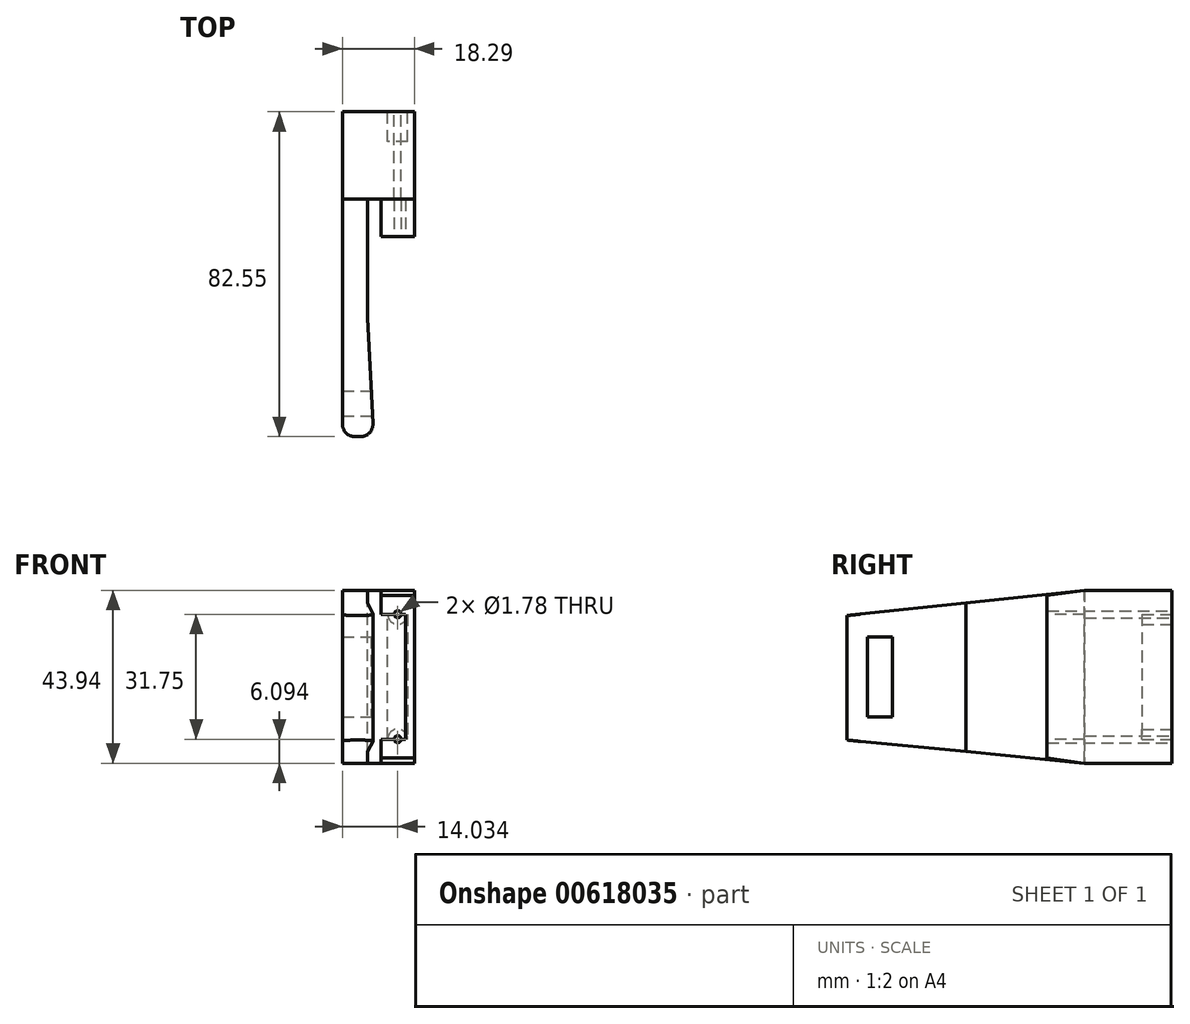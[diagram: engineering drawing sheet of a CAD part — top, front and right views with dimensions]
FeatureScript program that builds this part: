
annotation { "Feature Type Name" : "Feature", "Feature Type Description" : "" }
export const myFeature = defineFeature(function(context is Context, id is Id, definition is map)
    precondition{}
    {
        {
            var Q0;
            Q0=qCreatedBy(makeId("Right.planeOp"),FACE);
            var sketch = newSketch(context, id + "F0", { "sketchPlane" : qUnion([Q0])});
            skLineSegment(sketch, "E0", {"start": v(0, 0) * mm, "end": v(0, -43.94) * mm});
            skLineSegment(sketch, "E1", {"start": v(0, -43.94) * mm, "end": v(31.75, -43.94) * mm});
            skLineSegment(sketch, "E2", {"start": v(31.75, -43.94) * mm, "end": v(31.75, 0) * mm});
            skLineSegment(sketch, "E3", {"start": v(31.75, 0) * mm, "end": v(0, 0) * mm});
            skSolve(sketch);
        }
        {
            var Q0;
            Q0=qSketchRegion(id+"F0",true);
            extrude(context, id + "F1", {"entities" : qUnion([Q0]), "depth" : 8.5 * mm});
        }
        {
            var Q0;
            Q0=makeQuery(id+"F1.opExtrude","CAP_FACE",FACE,{"disambiguationData":[OSD([sQuery(id+"F0.wireOp",EDGE,"E0"),sQuery(id+"F0.wireOp",EDGE,"E1"),sQuery(id+"F0.wireOp",EDGE,"E2"),sQuery(id+"F0.wireOp",EDGE,"E3")])],"isStart":true});
            var sketch = newSketch(context, id + "F2", { "sketchPlane" : qUnion([Q0])});
            skLineSegment(sketch, "E4", {"start": v(-31.75, 0) * mm, "end": v(-9.53, 0) * mm});
            skLineSegment(sketch, "E5", {"start": v(-31.75, -21.97) * mm, "end": v(-9.53, -21.97) * mm});
            skLineSegment(sketch, "E6", {"start": v(0, -1.33) * mm, "end": v(0, -42.6) * mm});
            skLineSegment(sketch, "E7", {"start": v(0, -1.33) * mm, "end": v(-9.53, 0) * mm});
            skLineSegment(sketch, "E8", {"start": v(-31.75, -43.94) * mm, "end": v(-9.53, -43.94) * mm});
            skLineSegment(sketch, "E9", {"start": v(-9.53, -43.94) * mm, "end": v(0, -42.6) * mm});
            skSolve(sketch);
        }
        {
            var Q0;
            {var subQ0=sQuery(id+"F2.wireOp",EDGE,"E7");Q0=makeQuery(id+"F2.imprint","IMPRINT",FACE,{"disambiguationData":[TD([[makeQuery(id+"F2.imprint","IMPRINT",EDGE,{"derivedFrom":subQ0}),-1.0]])]});}
            var Q1;
            {var subQ0=sQuery(id+"F2.wireOp",EDGE,"E9");Q1=makeQuery(id+"F2.imprint","IMPRINT",FACE,{"disambiguationData":[TD([[makeQuery(id+"F2.imprint","IMPRINT",EDGE,{"derivedFrom":subQ0}),-1.0]])]});}
            extrude(context, id + "F3", {"entities" : qUnion([Q0, Q1]), "operationType" : NewBodyOperationType.REMOVE, "oppositeDirection" : true, "depth" : 25.4 * mm});
        }
        {
            var Q0;
            Q0=makeQuery(id+"F1.opExtrude","SWEPT_FACE",FACE,{"disambiguationData":[OSD([sQuery(id+"F0.wireOp",EDGE,"E2")])]});
            var sketch = newSketch(context, id + "F4", { "sketchPlane" : qUnion([Q0])});
            skCircle(sketch, "E10", {"center": v(-4.25, -37.85) * mm, "radius": 0.89 * mm});
            skCircle(sketch, "E11", {"center": v(-4.25, -6.1) * mm, "radius": 0.89 * mm});
            skSolve(sketch);
        }
        {
            var Q0;
            Q0=makeQuery(id+"F4.imprint","IMPRINT",FACE,{"disambiguationData":[TD([[makeQuery(id+"F4.imprint","IMPRINT",EDGE,{"derivedFrom":sQuery(id+"F4.wireOp",EDGE,"E10")}),1.0]])]});
            var Q1;
            Q1=makeQuery(id+"F4.imprint","IMPRINT",FACE,{"disambiguationData":[TD([[makeQuery(id+"F4.imprint","IMPRINT",EDGE,{"derivedFrom":sQuery(id+"F4.wireOp",EDGE,"E11")}),1.0]])]});
            extrude(context, id + "F5", {"entities" : qUnion([Q0, Q1]), "operationType" : NewBodyOperationType.REMOVE, "oppositeDirection" : true, "depth" : 31.75 * mm});
        }
        {
            var Q0;
            Q0=makeQuery(id+"F1.opExtrude","SWEPT_FACE",FACE,{"disambiguationData":[OSD([sQuery(id+"F0.wireOp",EDGE,"E0")])]});
            var sketch = newSketch(context, id + "F6", { "sketchPlane" : qUnion([Q0])});
            skLineSegment(sketch, "E12", {"start": v(4.25, -37.85) * mm, "end": v(0, -37.85) * mm});
            skLineSegment(sketch, "E13", {"start": v(4.25, -37.85) * mm, "end": v(8.5, -37.85) * mm});
            skLineSegment(sketch, "E14", {"start": v(4.25, -6.1) * mm, "end": v(0, -6.1) * mm});
            skLineSegment(sketch, "E15", {"start": v(4.25, -6.1) * mm, "end": v(8.5, -6.1) * mm});
            skPoint(sketch, "E16.endSnap0", {"position": v(8.5, -21.97) * mm});
            skLineSegment(sketch, "E17", {"start": v(6.29, -21.97) * mm, "end": v(6.29, -37.85) * mm});
            skLineSegment(sketch, "E18", {"start": v(6.29, -21.97) * mm, "end": v(6.29, -6.1) * mm});
            skSolve(sketch);
        }
        {
            var Q0;
            Q0=qSketchRegion(id+"F6",true);
            var Q1;
            {var subQ4=sQuery(id+"F6.wireOp",EDGE,"E17");Q1=makeQuery(id+"F6.imprint","IMPRINT",FACE,{"disambiguationData":[TD([[makeQuery(id+"F6.imprint","IMPRINT",EDGE,{"derivedFrom":subQ4}),-1.0]])]});}
            extrude(context, id + "F7", {"entities" : qUnion([Q0, Q1]), "operationType" : NewBodyOperationType.REMOVE, "oppositeDirection" : true, "depth" : 9.52 * mm});
        }
        {
            var Q0;
            Q0=makeQuery(id+"F1.opExtrude","CAP_FACE",FACE,{"disambiguationData":[OSD([sQuery(id+"F0.wireOp",EDGE,"E0"),sQuery(id+"F0.wireOp",EDGE,"E1"),sQuery(id+"F0.wireOp",EDGE,"E2"),sQuery(id+"F0.wireOp",EDGE,"E3")])],"isStart":true});
            var sketch = newSketch(context, id + "F8", { "sketchPlane" : qUnion([Q0])});
            skLineSegment(sketch, "E19", {"start": v(-9.52, -6.1) * mm, "end": v(-9.53, 0) * mm});
            skLineSegment(sketch, "E20", {"start": v(-9.53, -37.85) * mm, "end": v(-9.53, -43.94) * mm});
            skSolve(sketch);
        }
        {
            var Q0;
            Q0=makeQuery(id+"F8.imprint","IMPRINT",FACE,{"disambiguationData":[TD([[makeQuery(id+"F8.imprint","IMPRINT",EDGE,{"derivedFrom":sQuery(id+"F8.wireOp",EDGE,"E19")}),1.0]])]});
            extrude(context, id + "F9", {"entities" : qUnion([Q0]), "operationType" : NewBodyOperationType.ADD, "depth" : 3.43 * mm});
        }
        {
            var Q0;
            Q0=makeQuery(id+"F9.opExtrude","CAP_FACE",FACE,{"disambiguationData":[OSD([sQuery(id+"F0.wireOp",EDGE,"E0"),sQuery(id+"F0.wireOp",EDGE,"E1"),sQuery(id+"F0.wireOp",EDGE,"E2"),sQuery(id+"F0.wireOp",EDGE,"E3"),sQuery(id+"F8.wireOp",EDGE,"E19"),sQuery(id+"F8.wireOp",EDGE,"E20")])],"isStart":false});
            extrude(context, id + "F10", {"entities" : qUnion([Q0]), "operationType" : NewBodyOperationType.ADD, "depth" : 6.35 * mm, "offsetDistance" : 25.4 * mm});
        }
        {
            var Q0;
            {var subQ0=sQuery(id+"F8.wireOp",EDGE,"E20");var subQ1=sQuery(id+"F8.wireOp",EDGE,"E19");var subQ2=sQuery(id+"F0.wireOp",EDGE,"E0");Q0=makeQuery(id+"F10.boolean.opBoolean","MERGE",FACE,{"derivedFrom":[makeQuery(id+"F9.boolean.opBoolean","MERGE",FACE,{"derivedFrom":[makeQuery(id+"F7.boolean.opBoolean","COPY",FACE,{"derivedFrom":makeQuery(id+"F7.opExtrude","CAP_FACE",FACE,{"disambiguationData":[OSD([subQ2,sQuery(id+"F4.wireOp",EDGE,"E10"),sQuery(id+"F4.wireOp",EDGE,"E11"),sQuery(id+"F6.wireOp",EDGE,"E12"),sQuery(id+"F6.wireOp",EDGE,"E13"),sQuery(id+"F6.wireOp",EDGE,"E14"),sQuery(id+"F6.wireOp",EDGE,"E15"),sQuery(id+"F6.wireOp",EDGE,"E17"),sQuery(id+"F6.wireOp",EDGE,"E18")])],"isStart":false})}),makeQuery(id+"F9.opExtrude","SWEPT_FACE",FACE,{"disambiguationData":[OSD([subQ2,subQ1,subQ0])]})]}),makeQuery(id+"F10.opExtrude","SWEPT_FACE",FACE,{"disambiguationData":[OSD([subQ2,subQ1,subQ0])]})]});}
            var sketch = newSketch(context, id + "F11", { "sketchPlane" : qUnion([Q0])});
            skLineSegment(sketch, "E21.bottom", {"start": v(-9.78, -43.94) * mm, "end": v(-3.43, -43.94) * mm});
            skLineSegment(sketch, "E21.top", {"start": v(-9.78, 0) * mm, "end": v(0, 0) * mm});
            skLineSegment(sketch, "E21.left", {"start": v(-9.78, -43.94) * mm, "end": v(-9.78, 0) * mm});
            skLineSegment(sketch, "E21.right", {"start": v(-3.43, -43.94) * mm, "end": v(-3.43, 0) * mm});
            skSolve(sketch);
        }
        {
            var Q0;
            Q0=makeQuery(id+"F11.imprint","IMPRINT",FACE,{"disambiguationData":[TD([[makeQuery(id+"F11.imprint","IMPRINT",EDGE,{"derivedFrom":sQuery(id+"F11.wireOp",EDGE,"E21.bottom")}),1.0]])]});
            extrude(context, id + "F12", {"entities" : qUnion([Q0]), "operationType" : NewBodyOperationType.ADD, "depth" : 60.32 * mm, "offsetDistance" : 25.4 * mm});
        }
        {
            var Q0;
            Q0=makeQuery(id+"F12.opExtrude","SWEPT_FACE",FACE,{"disambiguationData":[OSD([sQuery(id+"F11.wireOp",EDGE,"E21.right")])]});
            var sketch = newSketch(context, id + "F13", { "sketchPlane" : qUnion([Q0])});
            skLineSegment(sketch, "E22", {"start": v(9.53, -21.97) * mm, "end": v(-45.6, -21.97) * mm});
            skLineSegment(sketch, "E23", {"start": v(-45.6, -32.13) * mm, "end": v(-45.6, -11.81) * mm});
            skLineSegment(sketch, "E24.bottom", {"start": v(-45.6, -32.13) * mm, "end": v(-39.24, -32.13) * mm});
            skLineSegment(sketch, "E24.top", {"start": v(-45.6, -11.81) * mm, "end": v(-39.24, -11.81) * mm});
            skLineSegment(sketch, "E24.right", {"start": v(-39.24, -32.13) * mm, "end": v(-39.24, -11.81) * mm});
            skSolve(sketch);
        }
        {
            var Q0;
            {var subQ5=sQuery(id+"F13.wireOp",EDGE,"E24.bottom");Q0=makeQuery(id+"F13.imprint","IMPRINT",FACE,{"disambiguationData":[TD([[makeQuery(id+"F13.imprint","IMPRINT",EDGE,{"derivedFrom":subQ5}),1.0]])]});}
            var Q1;
            {var subQ5=sQuery(id+"F13.wireOp",EDGE,"E24.top");Q1=makeQuery(id+"F13.imprint","IMPRINT",FACE,{"disambiguationData":[TD([[makeQuery(id+"F13.imprint","IMPRINT",EDGE,{"derivedFrom":subQ5}),-1.0]])]});}
            extrude(context, id + "F14", {"entities" : qUnion([Q0, Q1]), "operationType" : NewBodyOperationType.REMOVE, "oppositeDirection" : true, "depth" : 6.35 * mm, "offsetDistance" : 25.4 * mm});
        }
        {
            var Q0;
            {var subQ0=sQuery(id+"F0.wireOp",EDGE,"E3");Q0=makeQuery(id+"F12.boolean.opBoolean","MERGE",FACE,{"derivedFrom":[makeQuery(id+"F10.boolean.opBoolean","MERGE",FACE,{"derivedFrom":[makeQuery(id+"F9.boolean.opBoolean","MERGE",FACE,{"derivedFrom":[makeQuery(id+"F1.opExtrude","SWEPT_FACE",FACE,{"disambiguationData":[OSD([subQ0])]}),makeQuery(id+"F9.opExtrude","SWEPT_FACE",FACE,{"disambiguationData":[OSD([subQ0])]})]}),makeQuery(id+"F10.opExtrude","SWEPT_FACE",FACE,{"disambiguationData":[OSD([subQ0])]})]}),makeQuery(id+"F12.opExtrude","SWEPT_FACE",FACE,{"disambiguationData":[OSD([sQuery(id+"F11.wireOp",EDGE,"E21.top")])]})]});}
            var sketch = newSketch(context, id + "F15", { "sketchPlane" : qUnion([Q0])});
            skLineSegment(sketch, "E25", {"start": v(-3.43, -50.8) * mm, "end": v(-1.84, -50.8) * mm});
            skLineSegment(sketch, "E26", {"start": v(-1.84, -50.8) * mm, "end": v(-3.43, -20.64) * mm});
            skSolve(sketch);
        }
        {
            var Q0;
            {var subQ0=sQuery(id+"F15.wireOp",EDGE,"E25");Q0=makeQuery(id+"F15.imprint","IMPRINT",FACE,{"disambiguationData":[TD([[makeQuery(id+"F15.imprint","IMPRINT",EDGE,{"derivedFrom":subQ0}),1.0]])]});}
            var Q1;
            {var subQ0=sQuery(id+"F0.wireOp",EDGE,"E1");Q1=makeQuery(id+"F12.boolean.opBoolean","MERGE",FACE,{"derivedFrom":[makeQuery(id+"F10.boolean.opBoolean","MERGE",FACE,{"derivedFrom":[makeQuery(id+"F9.boolean.opBoolean","MERGE",FACE,{"derivedFrom":[makeQuery(id+"F1.opExtrude","SWEPT_FACE",FACE,{"disambiguationData":[OSD([subQ0])]}),makeQuery(id+"F9.opExtrude","SWEPT_FACE",FACE,{"disambiguationData":[OSD([subQ0])]})]}),makeQuery(id+"F10.opExtrude","SWEPT_FACE",FACE,{"disambiguationData":[OSD([subQ0])]})]}),makeQuery(id+"F12.opExtrude","SWEPT_FACE",FACE,{"disambiguationData":[OSD([sQuery(id+"F11.wireOp",EDGE,"E21.bottom")])]})]});}
            extrude(context, id + "F16", {"entities" : qUnion([Q0]), "operationType" : NewBodyOperationType.ADD, "endBound" : BoundingType.UP_TO_SURFACE, "oppositeDirection" : true, "depth" : 25.4 * mm, "endBoundEntityFace" : qUnion([Q1]), "offsetDistance" : 25.4 * mm});
        }
        {
            var Q0;
            Q0=makeQuery(id+"F16.opExtrude","SWEPT_FACE",FACE,{"disambiguationData":[OSD([sQuery(id+"F11.wireOp",EDGE,"E21.top"),sQuery(id+"F11.wireOp",EDGE,"E21.right")])]});
            extrude(context, id + "F17", {"entities" : qUnion([Q0]), "operationType" : NewBodyOperationType.REMOVE, "oppositeDirection" : true, "depth" : 25.4 * mm, "offsetDistance" : 25.4 * mm});
        }
        {
            var Q0;
            Q0=makeQuery(id+"F12.boolean.opBoolean","MERGE",FACE,{"derivedFrom":[makeQuery(id+"F10.opExtrude","CAP_FACE",FACE,{"disambiguationData":[OSD([sQuery(id+"F0.wireOp",EDGE,"E0"),sQuery(id+"F0.wireOp",EDGE,"E1"),sQuery(id+"F0.wireOp",EDGE,"E2"),sQuery(id+"F0.wireOp",EDGE,"E3"),sQuery(id+"F8.wireOp",EDGE,"E19"),sQuery(id+"F8.wireOp",EDGE,"E20")])],"isStart":false}),makeQuery(id+"F12.opExtrude","SWEPT_FACE",FACE,{"disambiguationData":[OSD([sQuery(id+"F11.wireOp",EDGE,"E21.left")])]})]});
            var sketch = newSketch(context, id + "F18", { "sketchPlane" : qUnion([Q0])});
            skLineSegment(sketch, "E27", {"start": v(45.6, -11.81) * mm, "end": v(53.08, -11.81) * mm});
            skLineSegment(sketch, "E28", {"start": v(45.6, -32.13) * mm, "end": v(54.42, -32.13) * mm});
            skLineSegment(sketch, "E29", {"start": v(-31.75, -21.97) * mm, "end": v(-9.53, -21.97) * mm});
            skLineSegment(sketch, "E30", {"start": v(-9.53, -21.97) * mm, "end": v(-9.53, -57.6) * mm});
            skLineSegment(sketch, "E31", {"start": v(-9.53, -21.97) * mm, "end": v(-9.53, 19.64) * mm});
            skLineSegment(sketch, "E32", {"start": v(50.8, -6.44) * mm, "end": v(-9.53, 0) * mm});
            skPoint(sketch, "E32.endSnap0", {"position": v(-9.53, -1.17) * mm});
            skLineSegment(sketch, "E33", {"start": v(-9.53, -43.94) * mm, "end": v(50.8, -38.07) * mm});
            skSolve(sketch);
        }
        {
            var Q0;
            Q0 = qSketchRegion(id + "F18", true);
            var Q1;
            {var subQ0=sQuery(id+"F18.wireOp",EDGE,"E32");Q1=makeQuery(id+"F18.imprint","IMPRINT",FACE,{"disambiguationData":[TD([[makeQuery(id+"F18.imprint","IMPRINT",EDGE,{"derivedFrom":subQ0}),-1.0]])]});}
            var Q2;
            {var subQ0=sQuery(id+"F18.wireOp",EDGE,"E33");Q2=makeQuery(id+"F18.imprint","IMPRINT",FACE,{"disambiguationData":[TD([[makeQuery(id+"F18.imprint","IMPRINT",EDGE,{"derivedFrom":subQ0}),-1.0]])]});}
            extrude(context, id + "F19", {"entities" : qUnion([Q0, Q1, Q2]), "operationType" : NewBodyOperationType.REMOVE, "oppositeDirection" : true, "depth" : 9.52 * mm, "offsetDistance" : 25.4 * mm});
        }
        {
            var Q0;
            Q0=makeQuery(id+"F16.opExtrude","SWEPT_EDGE",EDGE,{"disambiguationData":[OSD([sQuery(id+"F15.wireOp",EDGE,"E25"),sQuery(id+"F15.wireOp",EDGE,"E26")])]});
            fillet(context, id + "F20", {"entities" : qUnion([Q0]), "radius" : 3.17 * mm, "tangentPropagation" : true, "allowEdgeOverflow" : false});
        }
        {
            var Q0;
            Q0=makeQuery(id+"F12.opExtrude","CAP_EDGE",EDGE,{"disambiguationData":[OSD([sQuery(id+"F11.wireOp",EDGE,"E21.left")])],"isStart":false});
            fillet(context, id + "F21", {"entities" : qUnion([Q0]), "radius" : 3.17 * mm, "tangentPropagation" : true, "allowEdgeOverflow" : false});
        }
        {
            var Q0;
            {var subQ0=sQuery(id+"F0.wireOp",EDGE,"E2");Q0=makeQuery(id+"F10.boolean.opBoolean","MERGE",FACE,{"derivedFrom":[makeQuery(id+"F9.boolean.opBoolean","MERGE",FACE,{"derivedFrom":[makeQuery(id+"F1.opExtrude","SWEPT_FACE",FACE,{"disambiguationData":[OSD([subQ0])]}),makeQuery(id+"F9.opExtrude","SWEPT_FACE",FACE,{"disambiguationData":[OSD([subQ0])]})]}),makeQuery(id+"F10.opExtrude","SWEPT_FACE",FACE,{"disambiguationData":[OSD([subQ0])]})]});}
            var sketch = newSketch(context, id + "F22", { "sketchPlane" : qUnion([Q0])});
            skCircle(sketch, "E34", {"center": v(-4.25, -6.1) * mm, "radius": 2.54 * mm});
            skCircle(sketch, "E35", {"center": v(-4.25, -37.85) * mm, "radius": 2.54 * mm});
            skLineSegment(sketch, "E36", {"start": v(-1.71, -37.85) * mm, "end": v(-1.71, -6.1) * mm});
            skLineSegment(sketch, "E37", {"start": v(-6.8, -6.1) * mm, "end": v(-6.8, -37.85) * mm});
            skSolve(sketch);
        }
        {
            var Q0;
            Q0=makeQuery(id+"F22.imprint","IMPRINT",FACE,{"disambiguationData":[TD([[makeQuery(id+"F22.imprint","IMPRINT",EDGE,{"derivedFrom":makeQuery(id+"F5.boolean.opBoolean","COPY",EDGE,{"derivedFrom":makeQuery(id+"F5.opExtrude","CAP_EDGE",EDGE,{"disambiguationData":[OSD([sQuery(id+"F4.wireOp",EDGE,"E11")])],"isStart":true})})}),-1.0]])]});
            var Q1;
            {var subQ0=sQuery(id+"F22.wireOp",EDGE,"E36");Q1=makeQuery(id+"F22.imprint","IMPRINT",FACE,{"disambiguationData":[TD([[makeQuery(id+"F22.imprint","IMPRINT",EDGE,{"derivedFrom":subQ0}),1.0]])]});}
            var Q2;
            Q2=makeQuery(id+"F22.imprint","IMPRINT",FACE,{"disambiguationData":[TD([[makeQuery(id+"F22.imprint","IMPRINT",EDGE,{"derivedFrom":makeQuery(id+"F5.boolean.opBoolean","COPY",EDGE,{"derivedFrom":makeQuery(id+"F5.opExtrude","CAP_EDGE",EDGE,{"disambiguationData":[OSD([sQuery(id+"F4.wireOp",EDGE,"E10")])],"isStart":true})})}),-1.0]])]});
            extrude(context, id + "F23", {"entities" : qUnion([Q0, Q1, Q2]), "operationType" : NewBodyOperationType.REMOVE, "oppositeDirection" : true, "depth" : 7.62 * mm, "offsetDistance" : 25.4 * mm});
        }
    });
